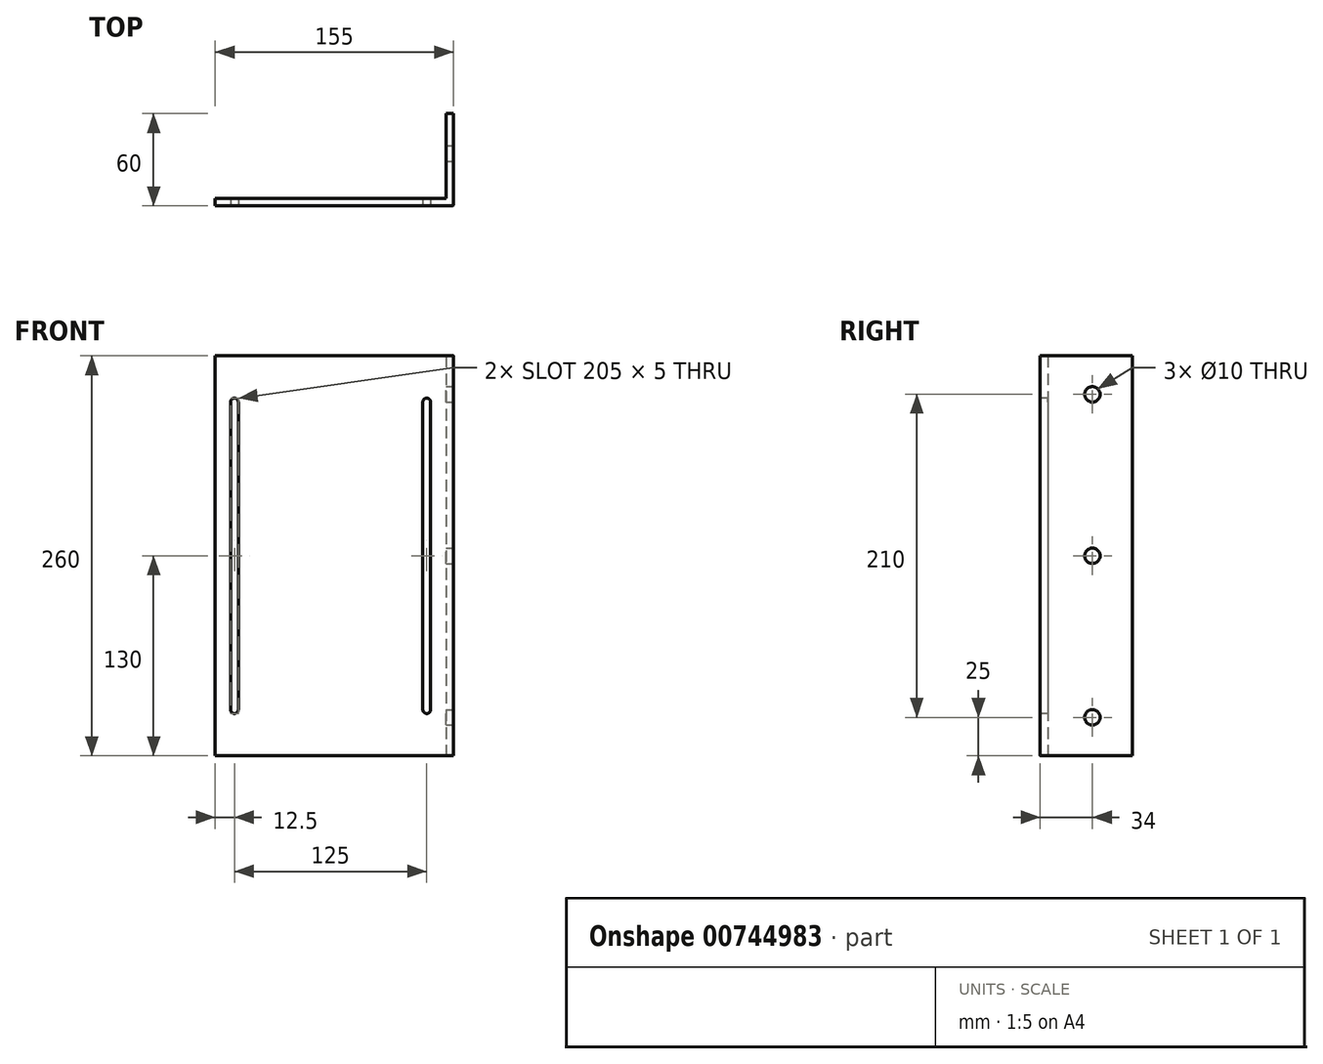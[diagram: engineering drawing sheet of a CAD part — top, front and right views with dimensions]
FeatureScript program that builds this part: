
annotation { "Feature Type Name" : "Feature", "Feature Type Description" : "" }
export const myFeature = defineFeature(function(context is Context, id is Id, definition is map)
    precondition{}
    {
        {
            var Q0;
            Q0=qCreatedBy(makeId("Front.planeOp"),FACE);
            var sketch = newSketch(context, id + "F0", { "sketchPlane" : qUnion([Q0])});
            skLineSegment(sketch, "E0.bottom", {"start": v(-75, 130) * mm, "end": v(75, 130) * mm});
            skLineSegment(sketch, "E0.top", {"start": v(-75, -130) * mm, "end": v(75, -130) * mm});
            skLineSegment(sketch, "E0.left", {"start": v(-75, 130) * mm, "end": v(-75, -130) * mm});
            skLineSegment(sketch, "E0.right", {"start": v(75, 130) * mm, "end": v(75, -130) * mm});
            skSolve(sketch);
        }
        {
            var Q0;
            Q0=makeQuery(id+"F0.imprint","IMPRINT",FACE,{"disambiguationData":[TD([[makeQuery(id+"F0.imprint","IMPRINT",EDGE,{"derivedFrom":sQuery(id+"F0.wireOp",EDGE,"E0.bottom")}),-1.0]])]});
            extrude(context, id + "F1", {"entities" : qUnion([Q0]), "oppositeDirection" : true, "depth" : 5 * mm, "offsetDistance" : 25 * mm});
        }
        {
            var Q0;
            Q0=makeQuery(id+"F1.opExtrude","CAP_FACE",FACE,{"disambiguationData":[OSD([sQuery(id+"F0.wireOp",EDGE,"E0.bottom"),sQuery(id+"F0.wireOp",EDGE,"E0.top"),sQuery(id+"F0.wireOp",EDGE,"E0.left"),sQuery(id+"F0.wireOp",EDGE,"E0.right")])],"isStart":true});
            var sketch = newSketch(context, id + "F2", { "sketchPlane" : qUnion([Q0])});
            skLineSegment(sketch, "E1.bottom", {"start": v(-65, 100) * mm, "end": v(-60, 100) * mm});
            skLineSegment(sketch, "E1.top", {"start": v(-65, -100) * mm, "end": v(-60, -100) * mm});
            skLineSegment(sketch, "E1.left", {"start": v(-65, 100) * mm, "end": v(-65, -100) * mm});
            skLineSegment(sketch, "E1.right", {"start": v(-60, 100) * mm, "end": v(-60, -100) * mm});
            skCircle(sketch, "E2", {"center": v(-62.5, 100) * mm, "radius": 2.5 * mm});
            skCircle(sketch, "E3", {"center": v(-62.5, -100) * mm, "radius": 2.5 * mm});
            skSolve(sketch);
        }
        {
            var Q0;
            Q0 = qSketchRegion(id + "F2", true);
            extrude(context, id + "F3", {"entities" : qUnion([Q0]), "operationType" : NewBodyOperationType.REMOVE, "oppositeDirection" : true, "depth" : 6 * mm, "offsetDistance" : 25 * mm});
        }
        {
            var Q0;
            Q0=makeQuery(id+"F1.opExtrude","CAP_FACE",FACE,{"disambiguationData":[OSD([sQuery(id+"F0.wireOp",EDGE,"E0.bottom"),sQuery(id+"F0.wireOp",EDGE,"E0.top"),sQuery(id+"F0.wireOp",EDGE,"E0.left"),sQuery(id+"F0.wireOp",EDGE,"E0.right")])],"isStart":true});
            var sketch = newSketch(context, id + "F4", { "sketchPlane" : qUnion([Q0])});
            skLineSegment(sketch, "E4.bottom", {"start": v(60, 100) * mm, "end": v(65, 100) * mm});
            skLineSegment(sketch, "E4.top", {"start": v(60, -100) * mm, "end": v(65, -100) * mm});
            skLineSegment(sketch, "E4.left", {"start": v(60, 100) * mm, "end": v(60, -100) * mm});
            skLineSegment(sketch, "E4.right", {"start": v(65, 100) * mm, "end": v(65, -100) * mm});
            skCircle(sketch, "E5", {"center": v(62.5, 100) * mm, "radius": 2.5 * mm});
            skCircle(sketch, "E6", {"center": v(62.5, -100) * mm, "radius": 2.5 * mm});
            skSolve(sketch);
        }
        {
            var Q0;
            Q0 = qSketchRegion(id + "F4", true);
            extrude(context, id + "F5", {"entities" : qUnion([Q0]), "operationType" : NewBodyOperationType.REMOVE, "oppositeDirection" : true, "depth" : 6 * mm, "offsetDistance" : 25 * mm});
        }
        {
            var Q0;
            Q0 = qSketchRegion(id + "F4", true);
            extrude(context, id + "F6", {"entities" : qUnion([Q0]), "operationType" : NewBodyOperationType.REMOVE, "oppositeDirection" : true, "depth" : 6 * mm, "offsetDistance" : 25 * mm});
        }
        {
            var Q0;
            Q0 = qSketchRegion(id + "F2", true);
            extrude(context, id + "F7", {"entities" : qUnion([Q0]), "operationType" : NewBodyOperationType.REMOVE, "oppositeDirection" : true, "depth" : 6 * mm, "offsetDistance" : 25 * mm});
        }
        {
            var Q0;
            Q0 = qSketchRegion(id + "F4", true);
            extrude(context, id + "F8", {"entities" : qUnion([Q0]), "operationType" : NewBodyOperationType.REMOVE, "oppositeDirection" : true, "depth" : 6 * mm, "offsetDistance" : 25 * mm});
        }
        {
            var Q0;
            Q0=makeQuery(id+"F1.opExtrude","SWEPT_FACE",FACE,{"disambiguationData":[OSD([sQuery(id+"F0.wireOp",EDGE,"E0.right")])]});
            var sketch = newSketch(context, id + "F9", { "sketchPlane" : qUnion([Q0])});
            skLineSegment(sketch, "E7.bottom", {"start": v(0, 130) * mm, "end": v(60, 130) * mm});
            skLineSegment(sketch, "E7.top", {"start": v(0, -130) * mm, "end": v(60, -130) * mm});
            skLineSegment(sketch, "E7.left", {"start": v(0, 130) * mm, "end": v(0, -130) * mm});
            skLineSegment(sketch, "E7.right", {"start": v(60, 130) * mm, "end": v(60, -130) * mm});
            skSolve(sketch);
        }
        {
            var Q0;
            Q0 = qSketchRegion(id + "F9", true);
            extrude(context, id + "F10", {"entities" : qUnion([Q0]), "operationType" : NewBodyOperationType.ADD, "depth" : 5 * mm, "offsetDistance" : 25 * mm});
        }
        {
            var Q0;
            Q0=makeQuery(id+"F10.opExtrude","CAP_FACE",FACE,{"disambiguationData":[OSD([sQuery(id+"F9.wireOp",EDGE,"E7.bottom"),sQuery(id+"F9.wireOp",EDGE,"E7.top"),sQuery(id+"F9.wireOp",EDGE,"E7.left"),sQuery(id+"F9.wireOp",EDGE,"E7.right")])],"isStart":false});
            var sketch = newSketch(context, id + "F11", { "sketchPlane" : qUnion([Q0])});
            skCircle(sketch, "E8", {"center": v(34, 0) * mm, "radius": 5 * mm});
            skCircle(sketch, "E9", {"center": v(34, 105) * mm, "radius": 5 * mm});
            skCircle(sketch, "E10", {"center": v(34, -105) * mm, "radius": 5 * mm});
            skSolve(sketch);
        }
        {
            var Q0;
            Q0 = qSketchRegion(id + "F11", true);
            extrude(context, id + "F12", {"entities" : qUnion([Q0]), "operationType" : NewBodyOperationType.REMOVE, "oppositeDirection" : true, "depth" : 6 * mm, "offsetDistance" : 25 * mm});
        }
        {
            var Q0;
            Q0=makeQuery(id+"F10.opExtrude","CAP_EDGE",EDGE,{"disambiguationData":[OSD([sQuery(id+"F9.wireOp",EDGE,"E7.left")])],"isStart":false});
            fillet(context, id + "F13", {"entities" : qUnion([Q0]), "radius" : 1 * mm, "tangentPropagation" : true, "allowEdgeOverflow" : false});
        }
    });
